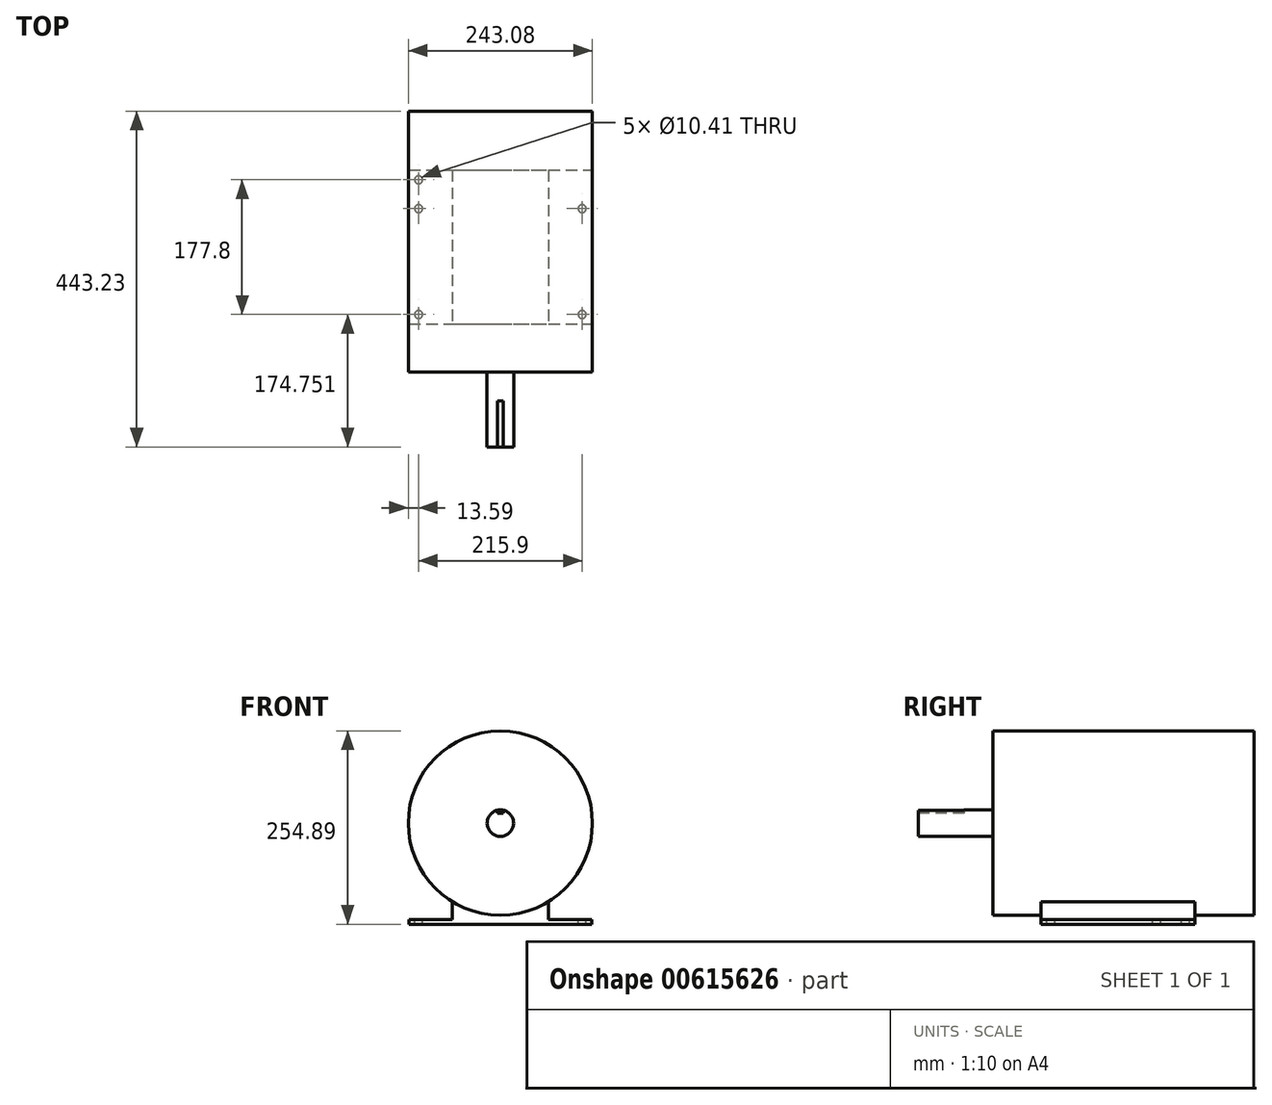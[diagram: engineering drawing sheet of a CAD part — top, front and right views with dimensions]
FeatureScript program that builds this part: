
annotation { "Feature Type Name" : "Feature", "Feature Type Description" : "" }
export const myFeature = defineFeature(function(context is Context, id is Id, definition is map)
    precondition{}
    {
        {
            var Q0;
            Q0=qCreatedBy(makeId("Front.planeOp"),FACE);
            var sketch = newSketch(context, id + "F0", { "sketchPlane" : qUnion([Q0])});
            skCircle(sketch, "E0", {"center": v(0, 0) * mm, "radius": 121.54 * mm});
            skSolve(sketch);
        }
        {
            var Q0;
            Q0 = qSketchRegion(id + "F0", true);
            extrude(context, id + "F1", {"entities" : qUnion([Q0]), "endBound" : BoundingType.SYMMETRIC, "depth" : 344.68 * mm, "offsetDistance" : 25.4 * mm});
        }
        {
            var Q0;
            Q0=makeQuery(id+"F1.opExtrude","CAP_FACE",FACE,{"disambiguationData":[OSD([sQuery(id+"F0.wireOp",EDGE,"E0")])],"isStart":false});
            var sketch = newSketch(context, id + "F2", { "sketchPlane" : qUnion([Q0])});
            skCircle(sketch, "E1", {"center": v(0, 0) * mm, "radius": 17.46 * mm});
            skSolve(sketch);
        }
        {
            var Q0;
            Q0 = qSketchRegion(id + "F2", true);
            extrude(context, id + "F3", {"entities" : qUnion([Q0]), "operationType" : NewBodyOperationType.ADD, "depth" : 98.55 * mm, "offsetDistance" : 25.4 * mm});
        }
        {
            var Q0;
            Q0=makeQuery(id+"F3.opExtrude","CAP_FACE",FACE,{"disambiguationData":[OSD([sQuery(id+"F2.wireOp",EDGE,"E1")])],"isStart":false});
            var sketch = newSketch(context, id + "F4", { "sketchPlane" : qUnion([Q0])});
            skLineSegment(sketch, "E2.bottom", {"start": v(-3.94, 20.95) * mm, "end": v(3.94, 20.95) * mm});
            skLineSegment(sketch, "E2.top", {"start": v(-3.94, 13.08) * mm, "end": v(3.94, 13.08) * mm});
            skLineSegment(sketch, "E2.left", {"start": v(-3.94, 20.95) * mm, "end": v(-3.94, 13.08) * mm});
            skLineSegment(sketch, "E2.right", {"start": v(3.94, 20.95) * mm, "end": v(3.94, 13.08) * mm});
            skLineSegment(sketch, "E3", {"start": v(0, 13.08) * mm, "end": v(0, 0) * mm, "construction": true});
            skPoint(sketch, "E4", {"position": v(-3.94, 17.01) * mm});
            skSolve(sketch);
        }
        {
            var Q0;
            Q0 = qSketchRegion(id + "F4", true);
            extrude(context, id + "F5", {"entities" : qUnion([Q0]), "operationType" : NewBodyOperationType.REMOVE, "oppositeDirection" : true, "depth" : 60.45 * mm, "offsetDistance" : 25.4 * mm});
        }
        {
            var Q0;
            Q0=makeQuery(id+"F3.opExtrude","CAP_FACE",FACE,{"disambiguationData":[OSD([sQuery(id+"F2.wireOp",EDGE,"E1")])],"isStart":false});
            cPlane(context, id + "F6", {"entities" : qUnion([Q0]), "cplaneType" : CPlaneType.OFFSET, "offset" : 162.05 * mm, "oppositeDirection" : true, "width" : 152.4 * mm, "height" : 152.4 * mm});
        }
        {
            var Q0;
            Q0=qCreatedBy(id+"F6.planeOp",FACE);
            var sketch = newSketch(context, id + "F7", { "sketchPlane" : qUnion([Q0])});
            skLineSegment(sketch, "E5.bottom", {"start": v(-120.65, -133.35) * mm, "end": v(120.65, -133.35) * mm});
            skLineSegment(sketch, "E5.top", {"start": v(-120.65, -127) * mm, "end": v(120.65, -127) * mm});
            skLineSegment(sketch, "E5.left", {"start": v(-120.65, -133.35) * mm, "end": v(-120.65, -127) * mm});
            skLineSegment(sketch, "E5.right", {"start": v(120.65, -133.35) * mm, "end": v(120.65, -127) * mm});
            skLineSegment(sketch, "E6", {"start": v(0, -127) * mm, "end": v(0, 0) * mm, "construction": true});
            skLineSegment(sketch, "E7", {"start": v(-63.5, -127) * mm, "end": v(-63.5, -103.63) * mm});
            skLineSegment(sketch, "E8.MirrorCS", {"start": v(63.5, -127) * mm, "end": v(63.5, -103.63) * mm});
            skArc(sketch, "E9", {"start": v(-63.5, -103.63) * mm, "mid": v(0, -121.54) * mm, "end": v(63.5, -103.63) * mm});
            skSolve(sketch);
        }
        {
            var Q0;
            Q0 = qSketchRegion(id + "F7", true);
            extrude(context, id + "F8", {"entities" : qUnion([Q0]), "operationType" : NewBodyOperationType.ADD, "oppositeDirection" : true, "depth" : 203.2 * mm, "offsetDistance" : 25.4 * mm});
        }
        {
            var Q0;
            {var subQ0=sQuery(id+"F7.wireOp",EDGE,"E5.top");Q0=makeQuery(id+"F8.opExtrude","SWEPT_FACE",FACE,{"disambiguationData":[OSD([subQ0]),TDD([makeQuery(id+"F7.imprint","IMPRINT",EDGE,{"disambiguationData":[TD([[makeQuery(id+"F7.imprint","INTERSECT",VERTEX,{"derivedFrom":[subQ0,sQuery(id+"F7.wireOp",EDGE,"E5.left")]}),-1.0]])],"derivedFrom":subQ0})])]});}
            var sketch = newSketch(context, id + "F9", { "sketchPlane" : qUnion([Q0])});
            skLineSegment(sketch, "E10.bottom", {"start": v(-107.95, -96.14) * mm, "end": v(107.95, -96.14) * mm, "construction": true});
            skLineSegment(sketch, "E10.top", {"start": v(-107.95, 81.66) * mm, "end": v(107.95, 81.66) * mm, "construction": true});
            skLineSegment(sketch, "E10.left", {"start": v(-107.95, 81.66) * mm, "end": v(-107.95, -96.14) * mm, "construction": true});
            skLineSegment(sketch, "E10.right", {"start": v(107.95, 81.66) * mm, "end": v(107.95, -96.14) * mm, "construction": true});
            skLineSegment(sketch, "E11", {"start": v(0, -96.14) * mm, "end": v(0, 0) * mm, "construction": true});
            skLineSegment(sketch, "E12", {"start": v(-107.95, 43.56) * mm, "end": v(107.95, 43.56) * mm, "construction": true});
            skSolve(sketch);
        }
        {
            var Q0;
            Q0=sQuery(id+"F9.wireOp",VERTEX,"E10.top.start");
            var Q1;
            Q1=sQuery(id+"F9.wireOp",VERTEX,"E12.start");
            var Q2;
            Q2=sQuery(id+"F9.wireOp",VERTEX,"E10.bottom.start");
            var Q3;
            Q3=sQuery(id+"F9.wireOp",VERTEX,"E10.bottom.end");
            var Q4;
            Q4=sQuery(id+"F9.wireOp",VERTEX,"E12.end");
            var Q5;
            Q5=sQuery(id+"F9.wireOp",VERTEX,"E10.right.end");
            var Q6;
            Q6=makeQuery(id+"F1.opExtrude","SWEPT_BODY",BODY,{"disambiguationData":[OSD([sQuery(id+"F0.wireOp",EDGE,"E0")])]});
            hole(context, id + "F10", {"style" : HoleStyle.SIMPLE, "endStyle" : HoleEndStyle.THROUGH, "holeDiameter" : 10.4 * mm, "majorDiameter" : 6.35 * mm, "isTappedThrough" : true, "tappedDepth" : 12.7 * mm, "tapClearance" : 3, "locations" : qUnion([Q0, Q1, Q2, Q3, Q4, Q5]), "scope" : qUnion([Q6])});
        }
    });
